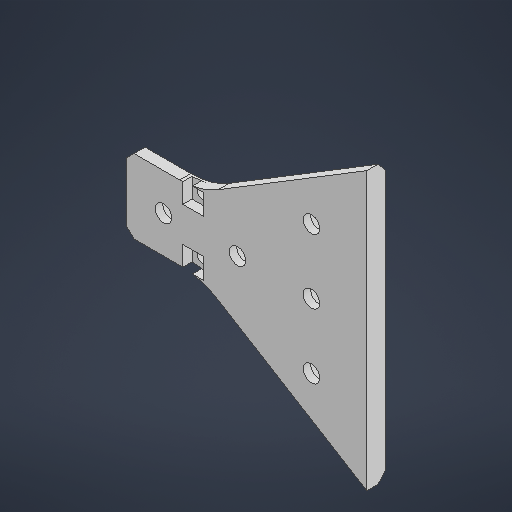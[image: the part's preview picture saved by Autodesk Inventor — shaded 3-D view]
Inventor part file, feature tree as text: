
AUTODESK INVENTOR PART (.ipt)
format: ipt  version: 2025.1 (Build 291241000, 241)  size: 563,200 bytes
history: native  units: mm
features: sketch x3, extrude x3, chamfer x2, hole x1, fillet x1, projected_geometry x1
ambient origin geometry x8: Origin, YZ Plane, XZ Plane, XY Plane, X Axis, Y Axis, Z Axis, Center Point
bodies: Solid1 (feature_tree)
feature tree (11):
  sketch  "Sketch1"  dims[d0=20.0mm d1=65.0mm]
  extrude  "Extrusion1"  Depth=20.0mm
  hole  "Hole1"  [1 undecoded]
  fillet  "Fillet1"  Radius=75.0mm
  chamfer  "Chamfer1"  Distance=5.0mm
  extrude  "Extrusion2"  Depth=20.0mm
  chamfer  "Chamfer2"  Distance=20.0mm
  extrude  "Extrusion4"  Depth=20.0mm TaperAngle=45.0deg
  sketch  "Sketch2"  dims[d2=50.0mm d4=20.0mm d5=75.0mm]
  projected_geometry  "Projected Loop1"
  sketch  "Sketch3"  dims[d6=35.0mm d7=5.0mm d8=0.0mm d9=40.0mm d10=4.5mm d11=6.0mm d12=8.0mm d13=3.0mm d14=90.0deg d15=8.0mm d16=20.594885mm d17=20.0mm d18=2.0mm d19=2.0mm d20=45.0deg d21=2.0mm d22=2.0mm d23=45.0deg d24=18.0mm d25=15.0mm d26=3.0mm d27=3.0mm d28=10.0mm d29=0.0mm d30=3.0mm d31=3.0mm d32=8.0mm d33=8.0mm d34=3.0mm d37=5.6mm d38=5.6mm d39=2.5mm d40=0.0mm d41=20.0mm]
note: 1 required parameter value undecoded (feature->parameter linkage not recoverable at this tier; creation-order binding heuristic only, values carry confidence <= 0.55)
